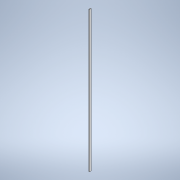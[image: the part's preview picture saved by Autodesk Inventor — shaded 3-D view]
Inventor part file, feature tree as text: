
AUTODESK INVENTOR PART (.ipt)
format: ipt  version: 2021 (Build 250183000, 183)  size: 93,696 bytes
history: native  units: mm
features: extrude x1, sketch x1
ambient origin geometry x8: Origin, YZ Plane, XZ Plane, XY Plane, X Axis, Y Axis, Z Axis, Center Point
bodies: Solid1 (feature_tree)
feature tree (2):
  extrude  "Extrusion1"  Depth=20.0mm
  sketch  "Sketch1"  dims[d0=10.0mm d1=20.0mm d2=1942.0mm d3=0.0mm]
